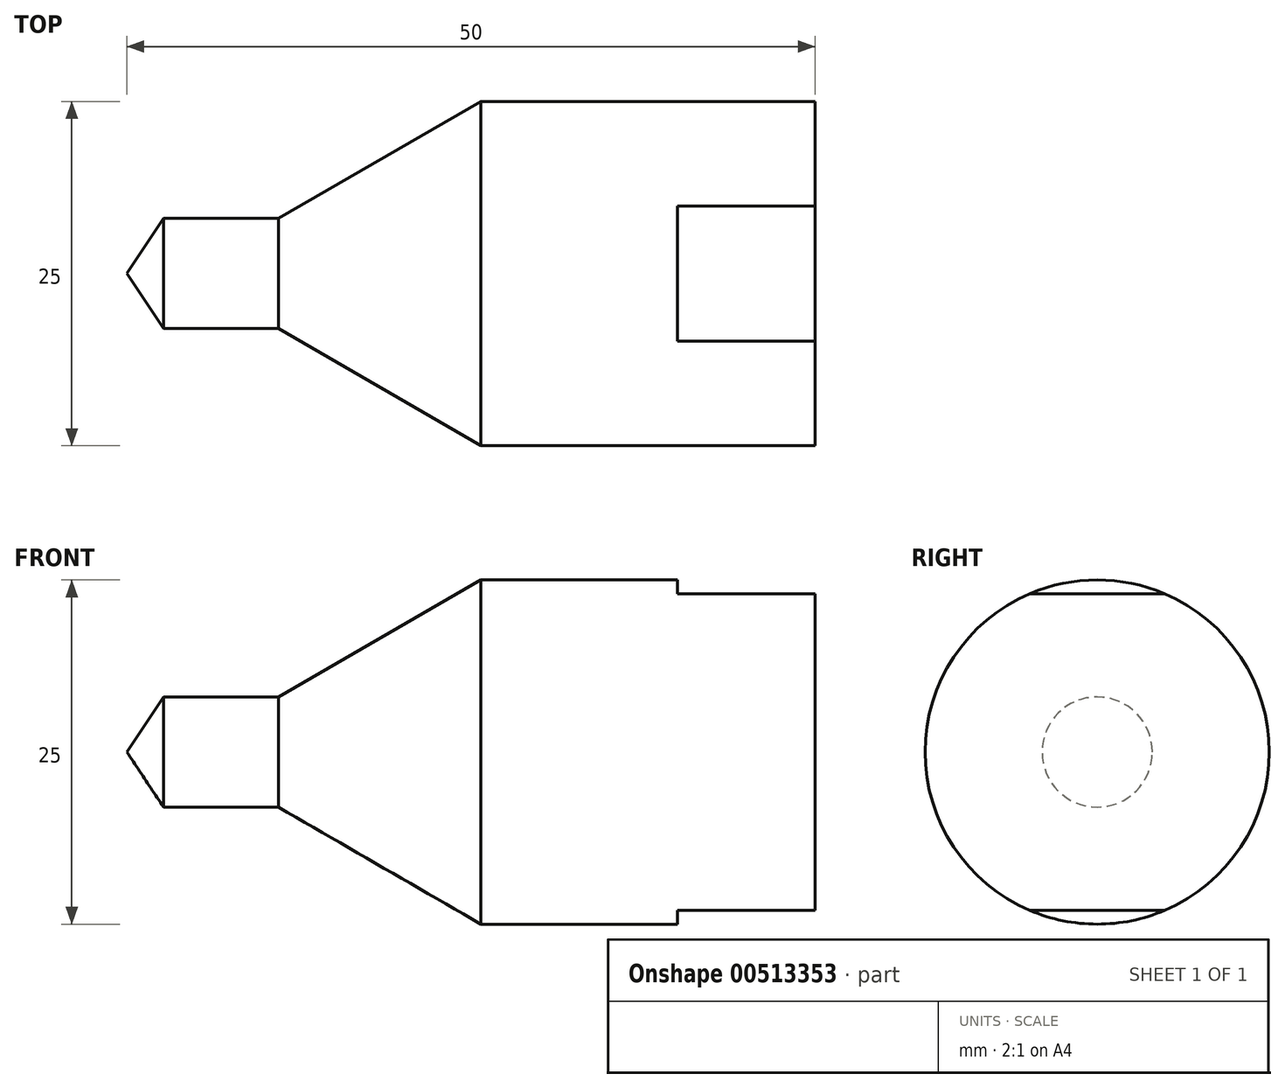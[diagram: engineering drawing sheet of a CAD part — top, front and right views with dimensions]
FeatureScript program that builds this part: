
annotation { "Feature Type Name" : "Feature", "Feature Type Description" : "" }
export const myFeature = defineFeature(function(context is Context, id is Id, definition is map)
    precondition{}
    {
        {
            var Q0;
            Q0=qCreatedBy(makeId("Front.planeOp"),FACE);
            var sketch = newSketch(context, id + "F0", { "sketchPlane" : qUnion([Q0])});
            skLineSegment(sketch, "E0", {"start": v(0, 0) * mm, "end": v(2.66, 4) * mm});
            skLineSegment(sketch, "E1", {"start": v(2.66, 4) * mm, "end": v(11, 4) * mm});
            skLineSegment(sketch, "E2", {"start": v(11, 4) * mm, "end": v(25.72, 12.5) * mm});
            skLineSegment(sketch, "E3", {"start": v(25.72, 12.5) * mm, "end": v(50, 12.5) * mm});
            skLineSegment(sketch, "E4", {"start": v(50, 12.5) * mm, "end": v(50, 0) * mm});
            skLineSegment(sketch, "E5", {"start": v(50, 0) * mm, "end": v(0, 0) * mm});
            skSolve(sketch);
        }
        {
            var Q0;
            Q0=makeQuery(id+"F0.imprint","IMPRINT",FACE,{"disambiguationData":[TD([[makeQuery(id+"F0.imprint","IMPRINT",EDGE,{"derivedFrom":sQuery(id+"F0.wireOp",EDGE,"E0")}),-1.0]])]});
            var Q1;
            Q1=sQuery(id+"F0.wireOp",EDGE,"E5");
            revolve(context, id + "F1", {"entities" : qUnion([Q0]), "axis" : qUnion([Q1]), "revolveType" : RevolveType.FULL});
        }
        {
            var Q0;
            Q0=qCreatedBy(makeId("Front.planeOp"),FACE);
            var sketch = newSketch(context, id + "F2", { "sketchPlane" : qUnion([Q0])});
            skLineSegment(sketch, "E6.bottom", {"start": v(40, 15.11) * mm, "end": v(53.42, 15.11) * mm});
            skLineSegment(sketch, "E6.top", {"start": v(40, 11.5) * mm, "end": v(53.42, 11.5) * mm});
            skLineSegment(sketch, "E6.left", {"start": v(40, 15.11) * mm, "end": v(40, 11.5) * mm});
            skLineSegment(sketch, "E6.right", {"start": v(53.42, 15.11) * mm, "end": v(53.42, 11.5) * mm});
            skLineSegment(sketch, "E7.MirrorCS", {"start": v(53.42, -15.11) * mm, "end": v(53.42, -11.5) * mm});
            skLineSegment(sketch, "E8.MirrorCS", {"start": v(40, -15.11) * mm, "end": v(40, -11.5) * mm});
            skLineSegment(sketch, "E9.MirrorCS", {"start": v(40, -15.11) * mm, "end": v(53.42, -15.11) * mm});
            skLineSegment(sketch, "E10.MirrorCS", {"start": v(40, -11.5) * mm, "end": v(53.42, -11.5) * mm});
            skSolve(sketch);
        }
        {
            var Q0;
            Q0=makeQuery(id+"F2.imprint","IMPRINT",FACE,{"disambiguationData":[TD([[makeQuery(id+"F2.imprint","IMPRINT",EDGE,{"derivedFrom":sQuery(id+"F2.wireOp",EDGE,"E6.bottom")}),-1.0]])]});
            var Q1;
            Q1=makeQuery(id+"F2.imprint","IMPRINT",FACE,{"disambiguationData":[TD([[makeQuery(id+"F2.imprint","IMPRINT",EDGE,{"derivedFrom":sQuery(id+"F2.wireOp",EDGE,"E7.MirrorCS")}),1.0]])]});
            extrude(context, id + "F3", {"entities" : qUnion([Q0, Q1]), "operationType" : NewBodyOperationType.REMOVE, "endBound" : BoundingType.SYMMETRIC, "depth" : 25 * mm});
        }
    });
